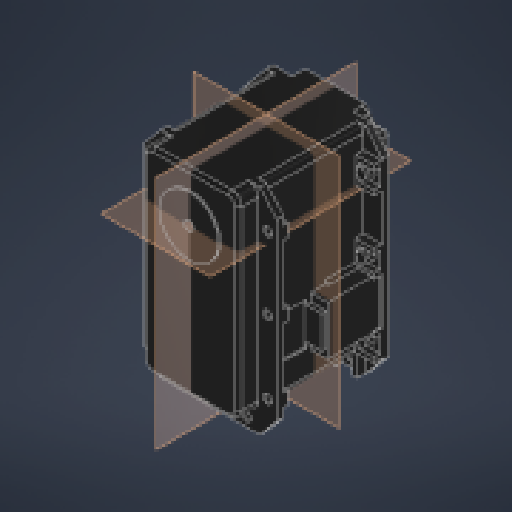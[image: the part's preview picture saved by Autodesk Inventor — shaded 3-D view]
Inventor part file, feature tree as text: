
AUTODESK INVENTOR PART (.ipt)
format: ipt  version: 2024 (Build 280153000, 153)  size: 416,768 bytes
history: native  units: mm
features: other x6, extrude x3, sketch x3, projected_geometry x2
ambient origin geometry x8: Origin, YZ Plane, XZ Plane, XY Plane, X Axis, Y Axis, Z Axis, Center Point
bodies: Body1 (feature_tree)
feature tree (14):
  other  "솔리드1"
  extrude  "돌출1"  Depth=2.5mm
  other  "작업 평면1"
  other  "작업 평면2"
  other  "작업 평면3"
  extrude  "돌출2"  Depth=80.0mm TaperAngle=360.0deg
  extrude  "돌출3"  Depth=2.5mm TaperAngle=0.0deg
  other  "스레드1"
  sketch  "스케치1"
  projected_geometry  "투영된 루프1"
  sketch  "스케치2"
  sketch  "스케치3"
  projected_geometry  "투영된 루프2"
  other  "기준1"
